# Revit family: 2023849
name_source: partatom
category: Lighting Fixtures
revit_build: Autodesk Revit 2018 (Build: 20170223_1515(x64)
units: mm (PartAtom-declared; Revit-internal decimal feet)

## family parameters
Cut with Voids When Loaded = No
Host = Face
Light Source = Yes
OmniClass Number = 23.80.70.00
OmniClass Title = Lighting
Part Type = Normal
Room Calculation Point = No
Round Connector Dimension = Use Diameter
Shared = No

## types (1)
- 2023849 OPTIX LIN R 1200 LUMI 4K ALU SSC
    Apparent Load = 31 VA
    Assembly Code = D5020200
    AssetType = Fixed
    ClassificationName = Uniclass2015
    ClassificationValue = EF_70_80
    Color Filter = 16777215
    Cost = 0 $
    Default Elevation = 1219 mm
    Description = OPTIX LINEAR RECESSED 1200 LUMI HCL 4000K ALU SSC is a ceiling recessed linear luminaire for office and education applications with Aluminised plastic extra low glare optics and RAL9016 colour fixture body.  SylSmart Standalone Office enabled.  4000K Neutral White LED, chromaticity tolerance of 3-step MacAdam ellipse. For 4000K - Colour rendering index Ra >98; Melanopic Ratio MEER: 0.778; Fidelity Index Rᶠ: 94; Gamut Index Rᶢ: 98. For 4000K luminous flux: 2850lm. Power consumption: 31W. Luminaire efficacy: 92lm/W. UGR<19 Luminance at 65°<200 Cd/m2, IK07, IP20. Photobiological safety risk group 0. Electrical protection Class I. Glow wire test 850°C. 60,000hrs L80B20 lifespan.
    Dimming Lamp Color Temperature Shift = <None>
    DocumentationLiterature = http://www.sylvania-lighting.com
    ElectricShockClassification = 93
    Emit Shape Visible in Rendering = No
    Emit from Circle Diameter = 610 mm
    Height = 86 mm  [stored 0.282152 ft]
    IfcExportAs = Class I
    IfcExportType = IfcLightFixtureType
    ImpactProtectionIndex = IfcLightFixtureType
    IngressProtection = IfcLightFixtureType
    InputNominalFrequency = 4000
    InputVoltage = 0
    LampColourRenderingIndex = 16500
    LampColourTemperature = LED
    LampMacAdamStep = 98
    LampNominalLuminous = 4000 K
    Length = 1130 mm  [stored 3.70735 ft]
    LightOutputRatio = LED
    LuminaireType = 0
    ManufacturerName = 93 lm/W
    Material = Feilo Sylvania
    Material_1_SYL = <By Category>
    Material_2_SYL = <By Category>
    Material_3_SYL = <By Category>
    Material_4_SYL = <By Category>
    Model = OPTIX LINEAR RECESSED 1200 LUMI 4K ALU SSC
    ModelNumber = 2023849
    ModelReference = OPTIX LINEAR RECESSED 1200 LUMI 4K ALU SSC
    Name = OPTIX LINEAR RECESSED 1200 LUMI 4K ALU SSC
    NominalDepth = 0 mm  [stored 0 ft]
    NominalHeight = 0 mm  [stored 0 ft]
    NominalLength = 95 mm
    Photometric Web File = 2023849.ies
    PowerConsumption = Lighting
    PowerFactor = 0
    Tilt Angle = -90.00°
    Type Image = <None>
    TypeName = OPTIX LINEAR RECESSED 1200 LUMI 4K ALU SSC
    URL = 0.98
    Voltage = 0 V
    WarrantyDescription = http://www.sylvania-lighting.com
    Width = 90 mm  [stored 0.295276 ft]

note: [stored X ft] marks values corroborated as IEEE doubles in the binary element streams (Revit-internal decimal feet)

## geometry (parser evidence)
native form markers: Sweep x2
no freeform markers — native parametric forms only
